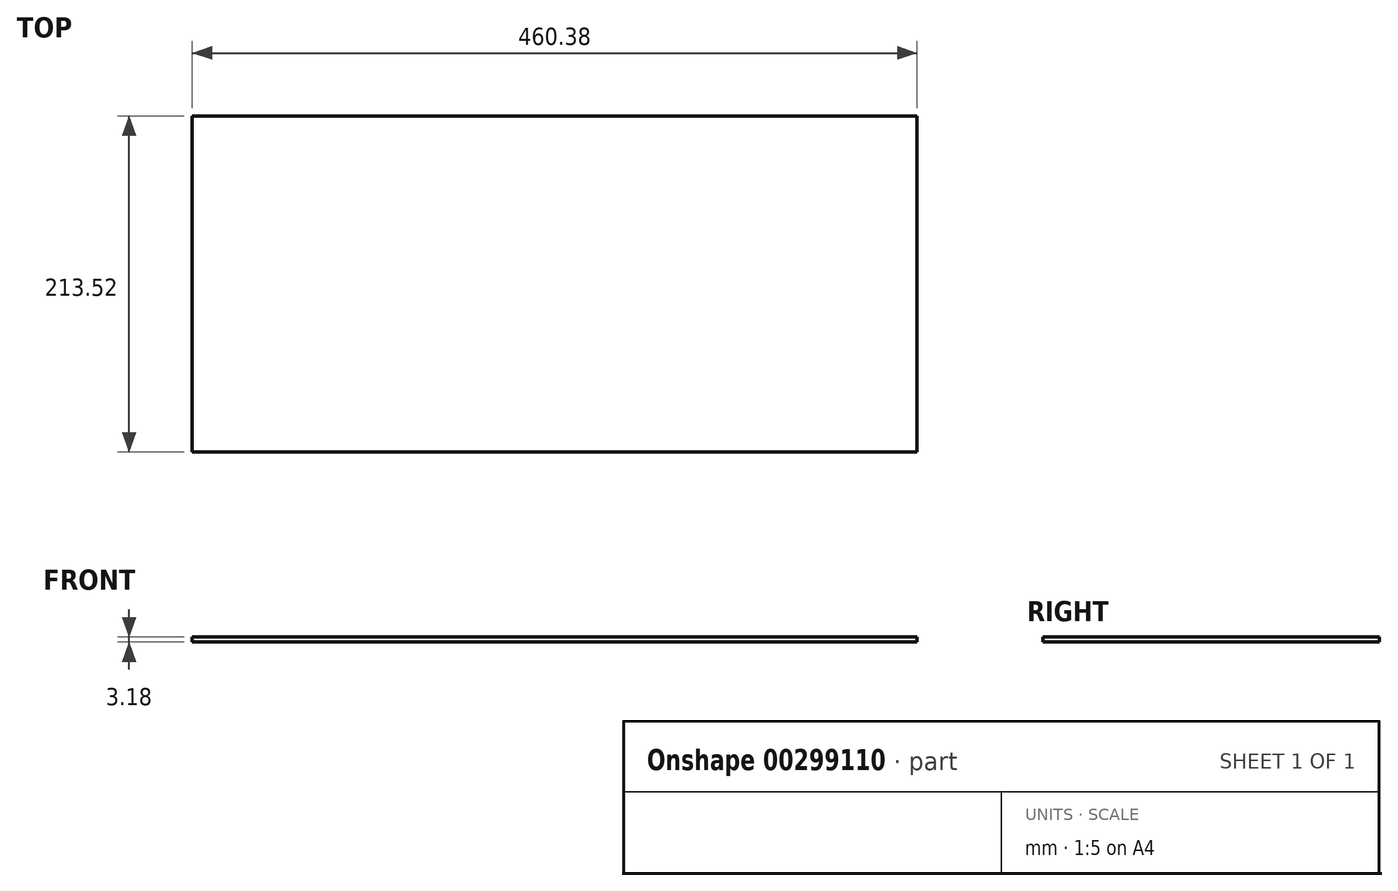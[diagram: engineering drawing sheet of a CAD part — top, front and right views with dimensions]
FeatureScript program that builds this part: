
annotation { "Feature Type Name" : "Feature", "Feature Type Description" : "" }
export const myFeature = defineFeature(function(context is Context, id is Id, definition is map)
    precondition{}
    {
        {
            var Q0;
            Q0=qCreatedBy(makeId("Front.planeOp"),FACE);
            var sketch = newSketch(context, id + "F0", { "sketchPlane" : qUnion([Q0])});
            skLineSegment(sketch, "E0.bottom", {"start": v(230.19, 1.59) * mm, "end": v(-230.19, 1.59) * mm});
            skLineSegment(sketch, "E0.top", {"start": v(230.19, -1.59) * mm, "end": v(-230.19, -1.59) * mm});
            skLineSegment(sketch, "E0.left", {"start": v(230.19, 1.59) * mm, "end": v(230.19, -1.59) * mm});
            skLineSegment(sketch, "E0.right", {"start": v(-230.19, 1.59) * mm, "end": v(-230.19, -1.59) * mm});
            skPoint(sketch, "E0.middle", {"position": v(0, 0) * mm});
            skSolve(sketch);
        }
        {
            var Q0;
            Q0 = qSketchRegion(id + "F0", true);
            extrude(context, id + "F1", {"entities" : qUnion([Q0]), "endBound" : BoundingType.SYMMETRIC, "depth" : 213.52 * mm});
        }
    });
